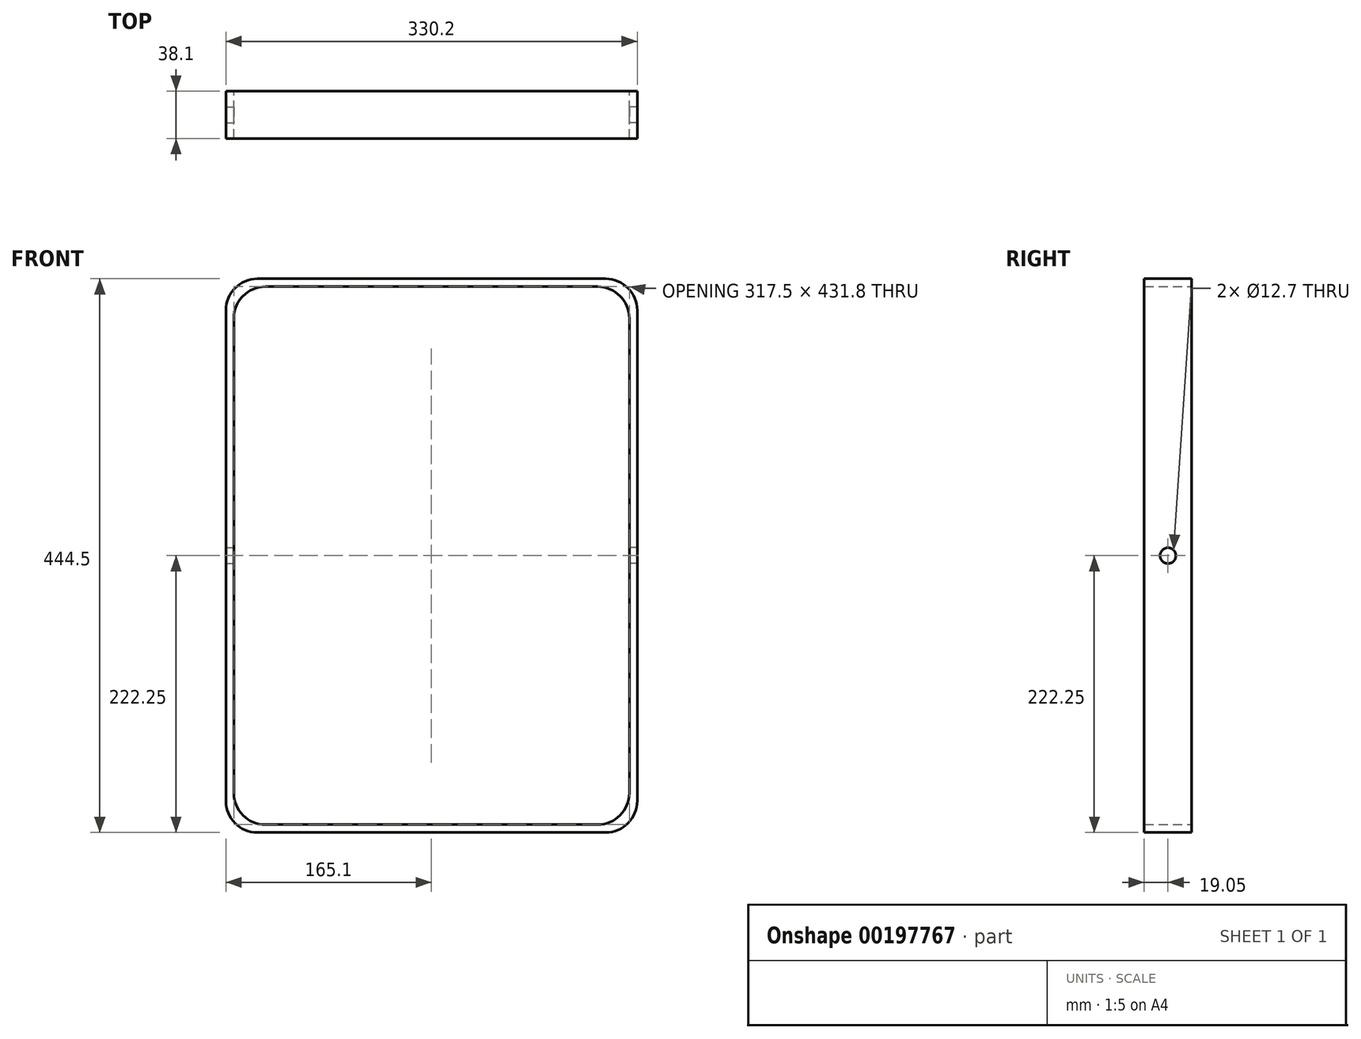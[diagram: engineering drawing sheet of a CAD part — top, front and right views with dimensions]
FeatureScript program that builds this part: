
annotation { "Feature Type Name" : "Feature", "Feature Type Description" : "" }
export const myFeature = defineFeature(function(context is Context, id is Id, definition is map)
    precondition{}
    {
        {
            var Q0;
            Q0=qCreatedBy(makeId("Front.planeOp"),FACE);
            var sketch = newSketch(context, id + "F0", { "sketchPlane" : qUnion([Q0])});
            skLineSegment(sketch, "E0.bottom", {"start": v(152.4, -152.4) * mm, "end": v(-152.4, -152.4) * mm});
            skLineSegment(sketch, "E0.top", {"start": v(152.4, 152.4) * mm, "end": v(-152.4, 152.4) * mm});
            skLineSegment(sketch, "E0.left", {"start": v(152.4, -152.4) * mm, "end": v(152.4, 152.4) * mm});
            skLineSegment(sketch, "E0.right", {"start": v(-152.4, -152.4) * mm, "end": v(-152.4, 152.4) * mm});
            skPoint(sketch, "E0.middle", {"position": v(0, 0) * mm});
            skPoint(sketch, "E1.top.start.orphan", {"position": v(50.8, 44.45) * mm});
            skPoint(sketch, "E1.right.end.orphan", {"position": v(-50.8, 44.45) * mm});
            skPoint(sketch, "E1.bottom.end.orphan", {"position": v(-50.8, -44.45) * mm});
            skPoint(sketch, "E1.bottom.start.orphan", {"position": v(50.8, -44.45) * mm});
            skLineSegment(sketch, "E2.bottom", {"start": v(158.75, -215.9) * mm, "end": v(-158.75, -215.9) * mm});
            skLineSegment(sketch, "E2.top", {"start": v(158.75, 215.9) * mm, "end": v(-158.75, 215.9) * mm});
            skLineSegment(sketch, "E2.left", {"start": v(158.75, -215.9) * mm, "end": v(158.75, 215.9) * mm});
            skLineSegment(sketch, "E2.right", {"start": v(-158.75, -215.9) * mm, "end": v(-158.75, 215.9) * mm});
            skLineSegment(sketch, "E3.bottom", {"start": v(165.1, -222.25) * mm, "end": v(-165.1, -222.25) * mm});
            skLineSegment(sketch, "E3.top", {"start": v(165.1, 222.25) * mm, "end": v(-165.1, 222.25) * mm});
            skLineSegment(sketch, "E3.left", {"start": v(165.1, -222.25) * mm, "end": v(165.1, 222.25) * mm});
            skLineSegment(sketch, "E3.right", {"start": v(-165.1, -222.25) * mm, "end": v(-165.1, 222.25) * mm});
            skSolve(sketch);
        }
        {
            var Q0;
            Q0=makeQuery(id+"F0.imprint","IMPRINT",FACE,{"disambiguationData":[TD([[makeQuery(id+"F0.imprint","IMPRINT",EDGE,{"derivedFrom":sQuery(id+"F0.wireOp",EDGE,"E2.bottom")}),1.0]])]});
            extrude(context, id + "F1", {"entities" : qUnion([Q0]), "depth" : 38.1 * mm});
        }
        {
            var Q0;
            Q0=makeQuery(id+"F1.opExtrude","SWEPT_EDGE",EDGE,{"disambiguationData":[OSD([sQuery(id+"F0.wireOp",EDGE,"E0.bottom"),sQuery(id+"F0.wireOp",EDGE,"E0.left")])]});
            var Q1;
            Q1=makeQuery(id+"F1.opExtrude","SWEPT_EDGE",EDGE,{"disambiguationData":[OSD([sQuery(id+"F0.wireOp",EDGE,"E0.bottom"),sQuery(id+"F0.wireOp",EDGE,"E0.right")])]});
            var Q2;
            Q2=makeQuery(id+"F1.opExtrude","SWEPT_EDGE",EDGE,{"disambiguationData":[OSD([sQuery(id+"F0.wireOp",EDGE,"E0.top"),sQuery(id+"F0.wireOp",EDGE,"E0.right")])]});
            var Q3;
            Q3=makeQuery(id+"F1.opExtrude","SWEPT_EDGE",EDGE,{"disambiguationData":[OSD([sQuery(id+"F0.wireOp",EDGE,"E0.top"),sQuery(id+"F0.wireOp",EDGE,"E0.left")])]});
            var Q4;
            Q4=makeQuery(id+"F1.opExtrude","SWEPT_EDGE",EDGE,{"disambiguationData":[OSD([sQuery(id+"F0.wireOp",EDGE,"E2.bottom"),sQuery(id+"F0.wireOp",EDGE,"E2.left")])]});
            var Q5;
            Q5=makeQuery(id+"F1.opExtrude","SWEPT_EDGE",EDGE,{"disambiguationData":[OSD([sQuery(id+"F0.wireOp",EDGE,"E2.top"),sQuery(id+"F0.wireOp",EDGE,"E2.left")])]});
            var Q6;
            Q6=makeQuery(id+"F1.opExtrude","SWEPT_EDGE",EDGE,{"disambiguationData":[OSD([sQuery(id+"F0.wireOp",EDGE,"E2.top"),sQuery(id+"F0.wireOp",EDGE,"E2.right")])]});
            var Q7;
            Q7=makeQuery(id+"F1.opExtrude","SWEPT_EDGE",EDGE,{"disambiguationData":[OSD([sQuery(id+"F0.wireOp",EDGE,"E2.bottom"),sQuery(id+"F0.wireOp",EDGE,"E2.right")])]});
            var Q8;
            Q8=makeQuery(id+"F1.opExtrude","SWEPT_EDGE",EDGE,{"disambiguationData":[OSD([sQuery(id+"F0.wireOp",EDGE,"E3.top"),sQuery(id+"F0.wireOp",EDGE,"E3.left")])]});
            var Q9;
            Q9=makeQuery(id+"F1.opExtrude","SWEPT_EDGE",EDGE,{"disambiguationData":[OSD([sQuery(id+"F0.wireOp",EDGE,"E3.bottom"),sQuery(id+"F0.wireOp",EDGE,"E3.left")])]});
            var Q10;
            Q10=makeQuery(id+"F1.opExtrude","SWEPT_EDGE",EDGE,{"disambiguationData":[OSD([sQuery(id+"F0.wireOp",EDGE,"E3.bottom"),sQuery(id+"F0.wireOp",EDGE,"E3.right")])]});
            var Q11;
            Q11=makeQuery(id+"F1.opExtrude","SWEPT_EDGE",EDGE,{"disambiguationData":[OSD([sQuery(id+"F0.wireOp",EDGE,"E3.top"),sQuery(id+"F0.wireOp",EDGE,"E3.right")])]});
            fillet(context, id + "F2", {"entities" : qUnion([Q0, Q1, Q2, Q3, Q4, Q5, Q6, Q7, Q8, Q9, Q10, Q11]), "radius" : 25.4 * mm, "tangentPropagation" : true, "allowEdgeOverflow" : false});
        }
        {
            var Q0;
            Q0=qCreatedBy(makeId("Right.planeOp"),FACE);
            var sketch = newSketch(context, id + "F5", { "sketchPlane" : qUnion([Q0])});
            skPoint(sketch, "E4", {"position": v(-19.05, 0) * mm});
            skSolve(sketch);
        }
        {
            var Q0;
            Q0=sQuery(id+"F5.wireOp",VERTEX,"E4");
            var Q1;
            Q1=makeQuery(id+"F1.opExtrude","SWEPT_BODY",BODY,{"disambiguationData":[OSD([sQuery(id+"F0.wireOp",EDGE,"E0.bottom"),sQuery(id+"F0.wireOp",EDGE,"E0.top"),sQuery(id+"F0.wireOp",EDGE,"E0.left"),sQuery(id+"F0.wireOp",EDGE,"E0.right"),sQuery(id+"F0.wireOp",EDGE,"E2.bottom"),sQuery(id+"F0.wireOp",EDGE,"E2.top"),sQuery(id+"F0.wireOp",EDGE,"E2.left"),sQuery(id+"F0.wireOp",EDGE,"E2.right")])]});
            hole(context, id + "F3", {"style" : HoleStyle.SIMPLE, "endStyle" : HoleEndStyle.THROUGH, "holeDiameter" : 12.7 * mm, "locations" : qUnion([Q0]), "scope" : qUnion([Q1]), "isTappedThrough" : true});
        }
        {
            var Q0;
            Q0=sQuery(id+"F5.wireOp",VERTEX,"E4");
            var Q1;
            Q1=makeQuery(id+"F1.opExtrude","SWEPT_BODY",BODY,{"disambiguationData":[OSD([sQuery(id+"F0.wireOp",EDGE,"E2.bottom"),sQuery(id+"F0.wireOp",EDGE,"E2.top"),sQuery(id+"F0.wireOp",EDGE,"E2.left"),sQuery(id+"F0.wireOp",EDGE,"E2.right"),sQuery(id+"F0.wireOp",EDGE,"E3.bottom"),sQuery(id+"F0.wireOp",EDGE,"E3.top"),sQuery(id+"F0.wireOp",EDGE,"E3.left"),sQuery(id+"F0.wireOp",EDGE,"E3.right")])]});
            hole(context, id + "F4", {"style" : HoleStyle.SIMPLE, "endStyle" : HoleEndStyle.THROUGH, "oppositeDirection" : true, "holeDiameter" : 12.7 * mm, "locations" : qUnion([Q0]), "scope" : qUnion([Q1]), "isTappedThrough" : true});
        }
    });
